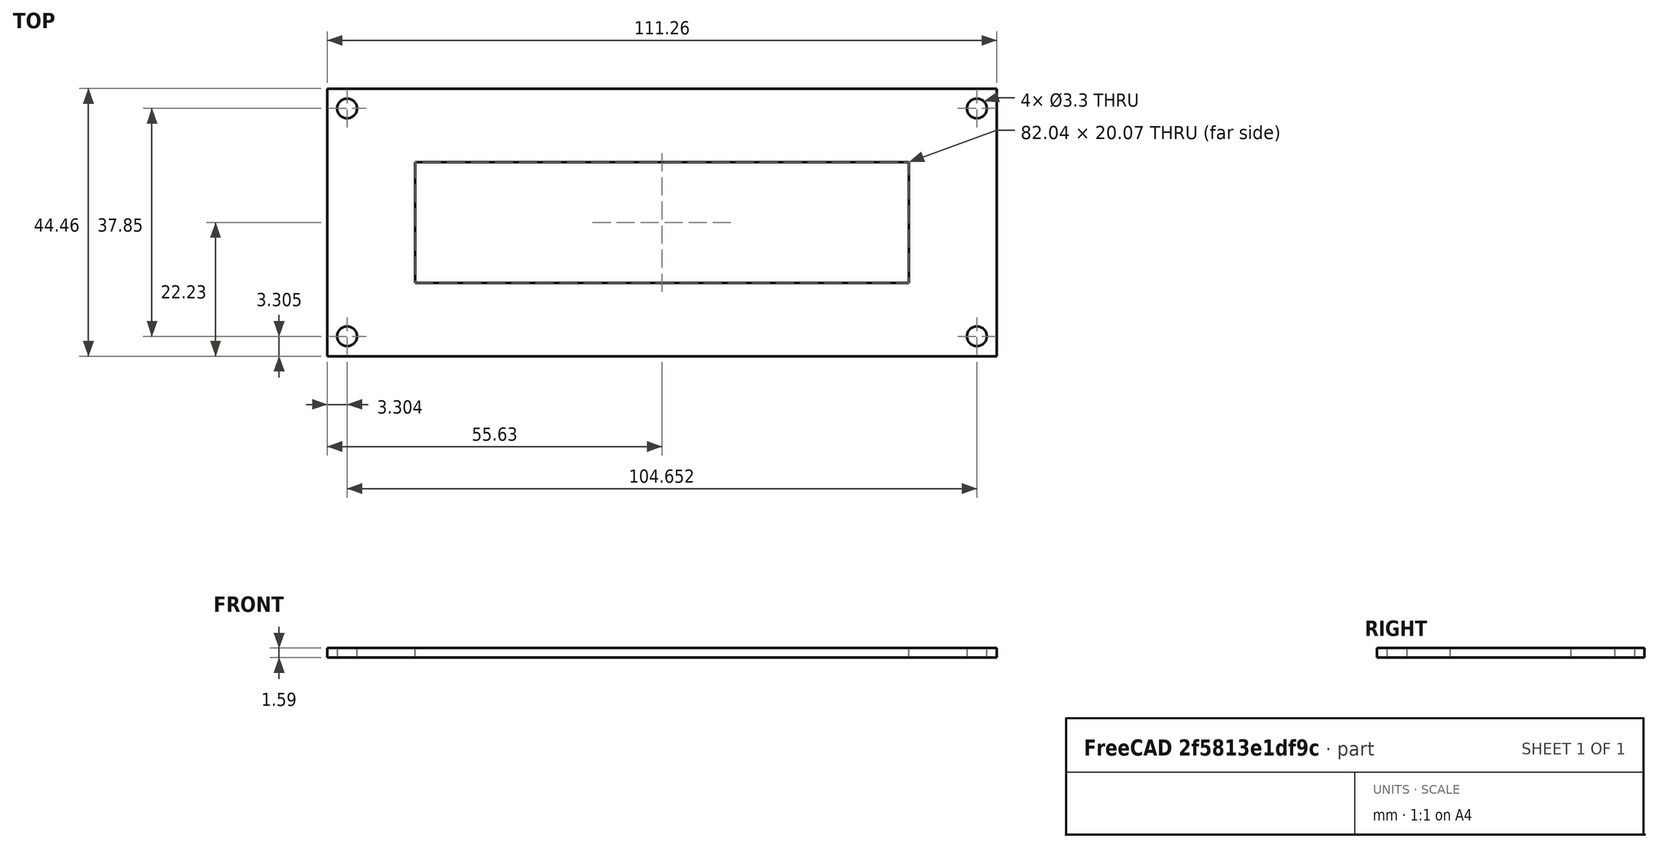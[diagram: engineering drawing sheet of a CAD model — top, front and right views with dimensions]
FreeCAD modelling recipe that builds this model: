
FCSTD DOCUMENT  (FreeCAD 0.19R24291 (Git))
Label: JackPanel_MJP
License: All rights reserved
LicenseURL: http://en.wikipedia.org/wiki/All_rights_reserved
objects: TechDraw::DrawViewDimension×8, TechDraw::DrawProjGroupItem×3, Sketcher::SketchObject×2, PartDesign::Pad×1, PartDesign::Pocket×1, PartDesign::Body×1, App::Part×1, Spreadsheet::Sheet×1, TechDraw::DrawSVGTemplate×1, TechDraw::DrawProjGroup×1, TechDraw::DrawViewAnnotation×1, TechDraw::DrawPage×1
note: 7 computed .brp shape members not serialized (recipe doc carries the construction recipe); baked Part::Feature solids carry a one-line shape summary decoded from their .brp

FEATURE [Sketcher::SketchObject] Sketch
  FullyConstrained = true
  MapMode = 5
  Support = -> [XY_Plane001]
  expr: Constraints[10] = <<SpreadsheetJackPanel>>.OverallHeight - 2 * 3.3mm
  expr: Constraints[9] = <<SpreadsheetJackPanel>>.OverallWidth - 2 * 3.3mm
  expr: Constraints[31] = <<SpreadsheetJackPanel>>.OverallHeight
  expr: Constraints[30] = <<SpreadsheetJackPanel>>.OverallWidth
  expr: Constraints[19] = <<SpreadsheetJackPanel>>.HorizontalCenter
  expr: Constraints[20] = <<SpreadsheetJackPanel>>.VerticalCenter
  sketch-geometry (13):
    g0: GeomPoint X=1 Y=1 Z=0
    g1: LineSegment StartX=-51.326 StartY=19.925 StartZ=0 EndX=53.326 EndY=19.925 EndZ=0
    g2: LineSegment StartX=53.326 StartY=19.925 StartZ=0 EndX=53.326 EndY=-17.925 EndZ=0
    g3: LineSegment StartX=53.326 StartY=-17.925 StartZ=0 EndX=-51.326 EndY=-17.925 EndZ=0
    g4: LineSegment StartX=-51.326 StartY=-17.925 StartZ=0 EndX=-51.326 EndY=19.925 EndZ=0
    g5: Circle CenterX=-51.326 CenterY=19.925 CenterZ=0 NormalX=0 NormalY=0 NormalZ=1 AngleXU=0 Radius=1.65
    g6: Circle CenterX=53.326 CenterY=-17.925 CenterZ=0 NormalX=0 NormalY=0 NormalZ=1 AngleXU=0 Radius=1.65
    g7: Circle CenterX=53.326 CenterY=19.925 CenterZ=0 NormalX=0 NormalY=0 NormalZ=1 AngleXU=0 Radius=1.65
    g8: Circle CenterX=-51.326 CenterY=-17.925 CenterZ=0 NormalX=0 NormalY=0 NormalZ=1 AngleXU=0 Radius=1.65
    g9: LineSegment StartX=-54.626 StartY=23.225 StartZ=0 EndX=56.626 EndY=23.225 EndZ=0
    g10: LineSegment StartX=56.626 StartY=23.225 StartZ=0 EndX=56.626 EndY=-21.225 EndZ=0
    g11: LineSegment StartX=56.626 StartY=-21.225 StartZ=0 EndX=-54.626 EndY=-21.225 EndZ=0
    g12: LineSegment StartX=-54.626 StartY=-21.225 StartZ=0 EndX=-54.626 EndY=23.225 EndZ=0
  constraints (32):
    c: Coincident(g1,g2)
    c: Coincident(g2,g3)
    c: Coincident(g3,g4)
    c: Coincident(g4,g1)
    c: Horizontal(g1)
    c: Horizontal(g3)
    c: Vertical(g2)
    c: Vertical(g4)
    c: Symmetric(g1,g2,g0)
    c: DistanceX(g3,g3) = 104.652
    c: DistanceY(g4,g4) = 37.85
    c: Coincident(g5,g1)
    c: Coincident(g6,g2)
    c: Coincident(g7,g1)
    c: Coincident(g8,g3)
    c: Diameter(g5) = 3.3
    c: Equal(g5,g8)
    c: Equal(g8,g6)
    c: Equal(g6,g7)
    c: DistanceX(g-1,g0) = 1
    c: DistanceY(g-1,g0) = 1
    c: Coincident(g9,g10)
    c: Coincident(g10,g11)
    c: Coincident(g11,g12)
    c: Coincident(g12,g9)
    c: Horizontal(g9)
    c: Horizontal(g11)
    c: Vertical(g10)
    c: Vertical(g12)
    c: Symmetric(g9,g10,g0)
    c: DistanceX(g11,g11) = 111.252
    c: DistanceY(g12,g12) = 44.45
FEATURE [PartDesign::Pad] Pad  label="PadJackPanelBase"
  Direction = (1,1,1)
  Length = 1.5875
  Length2 = 100
  Profile = -> Sketch
  Type = 0
  expr: Length = <<SpreadsheetJackPanel>>.Thickness
FEATURE [Sketcher::SketchObject] Sketch001
  FullyConstrained = true
  MapMode = 5
  Support = -> [XY_Plane001]
  expr: Constraints[42] = <<SpreadsheetJackPanel>>.CutoutHeight
  expr: Constraints[39] = Sketch.Constraints[31]
  expr: Constraints[38] = Sketch.Constraints[30]
  expr: Constraints[28] = Sketch.Constraints[20]
  expr: Constraints[23] = Sketch.Constraints[15]
  expr: Constraints[18] = Sketch.Constraints[10]
  expr: Constraints[41] = <<SpreadsheetJackPanel>>.CutoutWidth
  expr: Constraints[27] = Sketch.Constraints[19]
  expr: Constraints[17] = Sketch.Constraints[9]
  sketch-geometry (17):
    g0: LineSegment StartX=-40.021 StartY=11.033 StartZ=0 EndX=42.021 EndY=11.033 EndZ=0
    g1: LineSegment StartX=42.021 StartY=11.033 StartZ=0 EndX=42.021 EndY=-9.033 EndZ=0
    g2: LineSegment StartX=42.021 StartY=-9.033 StartZ=0 EndX=-40.021 EndY=-9.033 EndZ=0
    g3: LineSegment StartX=-40.021 StartY=-9.033 StartZ=0 EndX=-40.021 EndY=11.033 EndZ=0
    g4: GeomPoint X=1 Y=1 Z=0
    g5: LineSegment StartX=-51.326 StartY=19.925 StartZ=0 EndX=53.326 EndY=19.925 EndZ=0
    g6: LineSegment StartX=53.326 StartY=19.925 StartZ=0 EndX=53.326 EndY=-17.925 EndZ=0
    g7: LineSegment StartX=53.326 StartY=-17.925 StartZ=0 EndX=-51.326 EndY=-17.925 EndZ=0
    g8: LineSegment StartX=-51.326 StartY=-17.925 StartZ=0 EndX=-51.326 EndY=19.925 EndZ=0
    g9: Circle CenterX=-51.326 CenterY=19.925 CenterZ=0 NormalX=0 NormalY=0 NormalZ=1 AngleXU=0 Radius=1.65
    g10: Circle CenterX=53.326 CenterY=-17.925 CenterZ=0 NormalX=0 NormalY=0 NormalZ=1 AngleXU=0 Radius=1.65
    g11: Circle CenterX=53.326 CenterY=19.925 CenterZ=0 NormalX=0 NormalY=0 NormalZ=1 AngleXU=0 Radius=1.65
    g12: Circle CenterX=-51.326 CenterY=-17.925 CenterZ=0 NormalX=0 NormalY=0 NormalZ=1 AngleXU=0 Radius=1.65
    g13: LineSegment StartX=-54.626 StartY=23.225 StartZ=0 EndX=56.626 EndY=23.225 EndZ=0
    g14: LineSegment StartX=56.626 StartY=23.225 StartZ=0 EndX=56.626 EndY=-21.225 EndZ=0
    g15: LineSegment StartX=56.626 StartY=-21.225 StartZ=0 EndX=-54.626 EndY=-21.225 EndZ=0
    g16: LineSegment StartX=-54.626 StartY=-21.225 StartZ=0 EndX=-54.626 EndY=23.225 EndZ=0
  constraints (43):
    c: Coincident(g0,g1)
    c: Coincident(g1,g2)
    c: Coincident(g2,g3)
    c: Coincident(g3,g0)
    c: Horizontal(g0)
    c: Horizontal(g2)
    c: Vertical(g1)
    c: Vertical(g3)
    c: Coincident(g5,g6)
    c: Coincident(g6,g7)
    c: Coincident(g7,g8)
    c: Coincident(g8,g5)
    c: Horizontal(g5)
    c: Horizontal(g7)
    c: Vertical(g6)
    c: Vertical(g8)
    c: Symmetric(g5,g6,g4)
    c: DistanceX(g7,g7) = 104.652
    c: DistanceY(g8,g8) = 37.85
    c: Coincident(g9,g5)
    c: Coincident(g10,g6)
    c: Coincident(g11,g5)
    c: Coincident(g12,g7)
    c: Diameter(g9) = 3.3
    c: Equal(g9,g12)
    c: Equal(g12,g10)
    c: Equal(g10,g11)
    c: DistanceX(g-1,g4) = 1
    c: DistanceY(g-1,g4) = 1
    c: Coincident(g13,g14)
    c: Coincident(g14,g15)
    c: Coincident(g15,g16)
    c: Coincident(g16,g13)
    c: Horizontal(g13)
    c: Horizontal(g15)
    c: Vertical(g14)
    c: Vertical(g16)
    c: Symmetric(g13,g14,g4)
    c: DistanceX(g15,g15) = 111.252
    c: DistanceY(g16,g16) = 44.45
    c: Symmetric(g0,g1,g4)
    c: DistanceY(g3,g3) = 20.066
    c: DistanceX(g0,g0) = 82.042
FEATURE [PartDesign::Pocket] Pocket
  BaseFeature = -> Pad
  Length = 5
  Length2 = 100
  Profile = -> Sketch001
  Reversed = true
  Type = 1
FEATURE [PartDesign::Body] Body  label="BodyJP6"
  Group = -> [Sketch,Pad,Sketch001,Pocket]
  Origin = -> Origin001
  Tip = -> Pocket
FEATURE [App::Part] Part  label="Part_JP6"
  Group = -> [Body]
  Origin = -> Origin
FEATURE [Spreadsheet::Sheet] Spreadsheet  label="SpreadsheetJackPanel"
  cells = A1=Spreadsheet Jack Panel ; A2=For Omega MSS ; A3=MJP1-06-K; A5=HorizontalCenter; B5(HorizontalCenter)==1mm; A6=VerticalCenter; B6(VerticalCenter)==1mm; A8=OverallWidth; B8(OverallWidth)==4.38"; A9=OverallHeight; B9(OverallHeight)==1.75"; A10=Thickness; B10(Thickness)==0.0625in; A12=CutoutWidth; B12(CutoutWidth)==0.79"; A13=CutoutHeight; B13(CutoutHeight)==3.23"; A15=Clearance; B15(Clearance)==0.0625in; C15=Arbritary Given; A16=ClearanceCutoutWidth; B16(ClearanceCutoutWidth)==B12 + $B$15; C16=Calculated; A17=ClearanceCutoutHeight; B17(ClearanceCutoutHeight)==B13 + $B$15; C17=Calculated
FEATURE [TechDraw::DrawSVGTemplate] Template
  EditableTexts = Approved1=Approved 1; Approved2=Approved 2; CheckedBy=20230817; Code=Code; CompanyAddress=publicinvention.org; CompanyName=Public Invention; DrawingNumber=Drawing Number; DrawingTitle1=Thermocouple Jack Panel; DrawingTitle2=Six position; DrawingTitle3=MJP1-06-x; DrawnBy=Lee Erickson; Revision=Rev; Scale=1:1; Sheet=Sheet 1 of 1
  Height = 215.9
  Orientation = 1
  Width = 279.4
FEATURE [TechDraw::DrawProjGroupItem] ProjItem  label="Front"
  CoarseView = false
  Direction = (0,0,1)
  Focus = 100
  HardHidden = false
  IsoCount = 0
  IsoHidden = false
  IsoVisible = false
  LockPosition = true
  Perspective = false
  Rotation = 0
  RotationVector = (1,0,0)
  ScaleType = 2
  SeamHidden = false
  SeamVisible = true
  SmoothHidden = false
  SmoothVisible = true
  Source = -> [Body]
  Type = 0
  X = 0
  XDirection = (1,0,0)
  Y = 0
FEATURE [TechDraw::DrawProjGroupItem] ProjItem001  label="FrontTopRight"
  CoarseView = false
  Direction = (0.57735,0.57735,0.57735)
  Focus = 100
  HardHidden = false
  IsoCount = 0
  IsoHidden = false
  IsoVisible = false
  LockPosition = true
  Perspective = false
  Rotation = 0
  RotationVector = (1,0,0)
  ScaleType = 2
  SeamHidden = false
  SeamVisible = true
  SmoothHidden = false
  SmoothVisible = true
  Source = -> [Body]
  Type = 7
  X = 123.867
  XDirection = (0.707107,0,-0.707107)
  Y = 39.2148
FEATURE [TechDraw::DrawProjGroupItem] ProjItem002  label="Left"
  CoarseView = false
  Direction = (-1,0,1e-16)
  Focus = 100
  HardHidden = false
  IsoCount = 0
  IsoHidden = false
  IsoVisible = false
  LockPosition = true
  Perspective = false
  Rotation = 0
  RotationVector = (1,0,0)
  ScaleType = 2
  SeamHidden = false
  SeamVisible = true
  SmoothHidden = false
  SmoothVisible = true
  Source = -> [Body]
  Type = 1
  X = 71.4198
  XDirection = (1e-16,0,1)
  Y = 0
FEATURE [TechDraw::DrawProjGroup] ProjGroup
  Anchor = -> ProjItem
  AutoDistribute = true
  LockPosition = false
  ProjectionType = 0
  Rotation = 0
  ScaleType = 2
  Source = -> [Body]
  Views = -> [ProjItem,ProjItem001,ProjItem002]
  X = 88.3555
  Y = 106.078
  spacingX = 15
  spacingY = 15
FEATURE [TechDraw::DrawViewDimension] Dimension
  Arbitrary = false
  ArbitraryTolerances = false
  EqualTolerance = true
  FormatSpec = %.3f
  FormatSpecOverTolerance = %+.3f
  FormatSpecUnderTolerance = %+.3f
  Inverted = false
  LockPosition = false
  MeasureType = 1
  OverTolerance = 0
  References2D = -> [ProjItem]
  Rotation = 0
  ScaleType = 2
  TheoreticalExact = false
  Type = 1
  UnderTolerance = 0
  X = 1.06617
  Y = 5.85128
FEATURE [TechDraw::DrawViewDimension] Dimension001
  Arbitrary = false
  ArbitraryTolerances = false
  EqualTolerance = true
  FormatSpec = %.3f
  FormatSpecOverTolerance = %+.3f
  FormatSpecUnderTolerance = %+.3f
  Inverted = false
  LockPosition = false
  MeasureType = 1
  OverTolerance = 0
  References2D = -> [ProjItem]
  Rotation = 0
  ScaleType = 2
  TheoreticalExact = false
  Type = 2
  UnderTolerance = 0
  X = -36.4839
  Y = 47.9778
FEATURE [TechDraw::DrawViewDimension] Dimension002
  Arbitrary = false
  ArbitraryTolerances = false
  EqualTolerance = true
  FormatSpec = %.3f
  FormatSpecOverTolerance = %+.3f
  FormatSpecUnderTolerance = %+.3f
  Inverted = false
  LockPosition = false
  MeasureType = 1
  OverTolerance = 0
  References2D = -> [ProjItem]
  Rotation = 0
  ScaleType = 2
  TheoreticalExact = false
  Type = 2
  UnderTolerance = 0
  X = -65.9323
  Y = -0.710782
FEATURE [TechDraw::DrawViewDimension] Dimension003
  Arbitrary = false
  ArbitraryTolerances = false
  EqualTolerance = true
  FormatSpec = %.3f
  FormatSpecOverTolerance = %+.3f
  FormatSpecUnderTolerance = %+.3f
  Inverted = false
  LockPosition = false
  MeasureType = 1
  OverTolerance = 0
  References2D = -> [ProjItem]
  Rotation = 0
  ScaleType = 2
  TheoreticalExact = false
  Type = 1
  UnderTolerance = 0
  X = -0.485486
  Y = -33.8133
FEATURE [TechDraw::DrawViewDimension] Dimension004
  Arbitrary = false
  ArbitraryTolerances = false
  EqualTolerance = true
  FormatSpec = %.3f
  FormatSpecOverTolerance = %+.3f
  FormatSpecUnderTolerance = %+.3f
  Inverted = false
  LockPosition = false
  MeasureType = 1
  OverTolerance = 0
  References2D = -> [ProjItem]
  Rotation = 0
  ScaleType = 2
  TheoreticalExact = false
  Type = 1
  UnderTolerance = 0
  X = -0.225296
  Y = -25.9092
FEATURE [TechDraw::DrawViewDimension] Dimension005
  Arbitrary = false
  ArbitraryTolerances = false
  EqualTolerance = true
  FormatSpec = %.3f
  FormatSpecOverTolerance = %+.3f
  FormatSpecUnderTolerance = %+.3f
  Inverted = false
  LockPosition = false
  MeasureType = 1
  OverTolerance = 0
  References2D = -> [ProjItem]
  Rotation = 0
  ScaleType = 2
  TheoreticalExact = false
  Type = 2
  UnderTolerance = 0
  X = 55.7054
  Y = -0.225296
FEATURE [TechDraw::DrawViewDimension] Dimension006
  Arbitrary = false
  ArbitraryTolerances = false
  EqualTolerance = true
  FormatSpec = ⌀%.3f
  FormatSpecOverTolerance = %+.3f
  FormatSpecUnderTolerance = %+.3f
  Inverted = false
  LockPosition = false
  MeasureType = 1
  OverTolerance = 0
  References2D = -> [ProjItem]
  Rotation = 0
  ScaleType = 2
  TheoreticalExact = false
  Type = 5
  UnderTolerance = 0
  X = -51.818
  Y = 39.6521
FEATURE [TechDraw::DrawViewDimension] Dimension007
  Arbitrary = false
  ArbitraryTolerances = false
  EqualTolerance = true
  FormatSpec = %.3f
  FormatSpecOverTolerance = %+.3f
  FormatSpecUnderTolerance = %+.3f
  Inverted = false
  LockPosition = false
  MeasureType = 1
  OverTolerance = 0
  References2D = -> [ProjItem002]
  Rotation = 0
  ScaleType = 2
  TheoreticalExact = false
  Type = 1
  UnderTolerance = 0
  X = -13.6899
  Y = 38.5224
FEATURE [TechDraw::DrawViewAnnotation] Annotation
  Font = osifont
  LineSpace = 80
  LockPosition = false
  MaxWidth = -1
  Rotation = 0
  ScaleType = 2
  Text = Note: | Cut out is for MSS-06
  TextSize = 5.0038
  TextStyle = 0
  X = 54.3075
  Y = 43.2886
FEATURE [TechDraw::DrawPage] Page
  KeepUpdated = true
  NextBalloonIndex = 1
  ProjectionType = 0
  Template = -> Template
  Views = -> [ProjGroup,Dimension,Dimension001,Dimension002,Dimension003,Dimension004,Dimension005,Dimension006,Dimension007,Annotation]
